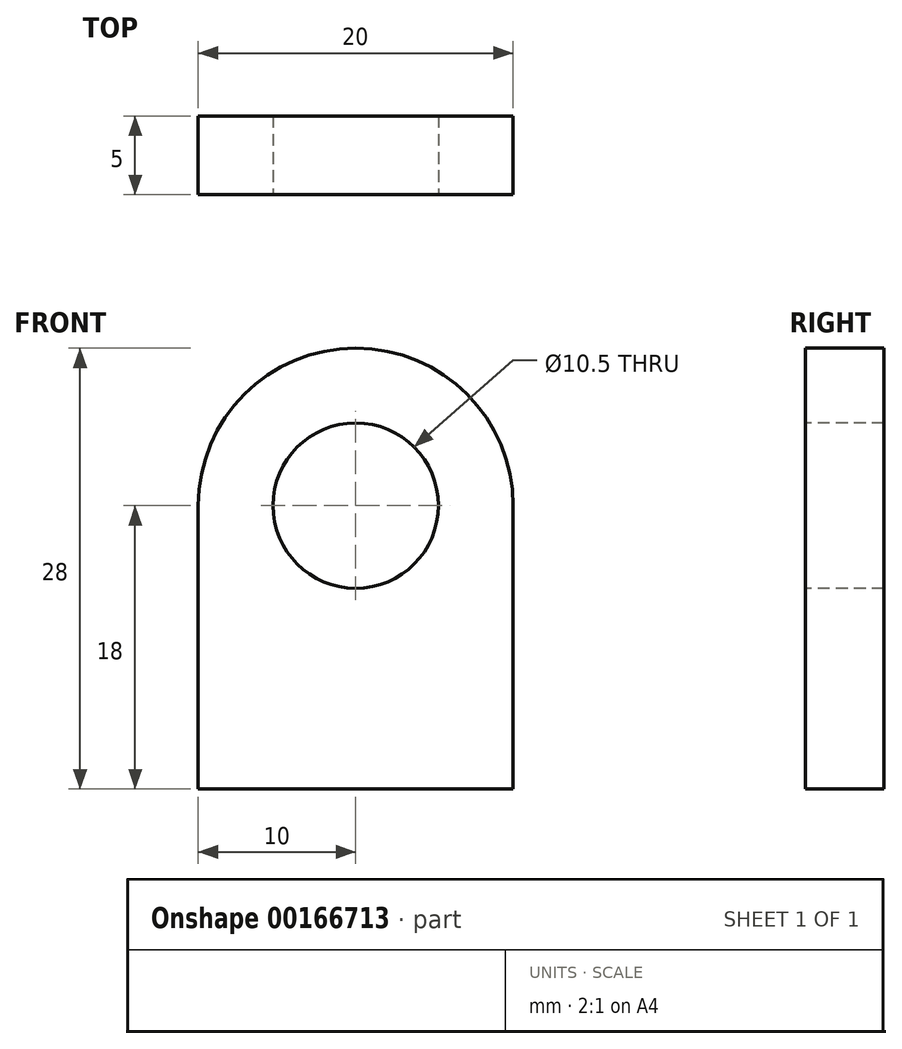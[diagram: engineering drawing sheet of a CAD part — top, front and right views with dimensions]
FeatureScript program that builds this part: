
annotation { "Feature Type Name" : "Feature", "Feature Type Description" : "" }
export const myFeature = defineFeature(function(context is Context, id is Id, definition is map)
    precondition{}
    {
        {
            var Q0;
            Q0=qCreatedBy(makeId("Front.planeOp"),FACE);
            var sketch = newSketch(context, id + "F0", { "sketchPlane" : qUnion([Q0])});
            skCircle(sketch, "E0", {"center": v(0, 0) * mm, "radius": 5.25 * mm});
            skCircle(sketch, "E1", {"center": v(0, 0) * mm, "radius": 10 * mm});
            skLineSegment(sketch, "E2", {"start": v(10, 0) * mm, "end": v(10, -18) * mm});
            skLineSegment(sketch, "E3", {"start": v(10, -18) * mm, "end": v(-10, -18) * mm});
            skLineSegment(sketch, "E4", {"start": v(-10, -18) * mm, "end": v(-10, 0) * mm});
            skSolve(sketch);
        }
        {
            var Q0;
            {var subQ0=sQuery(id+"F0.wireOp",EDGE,"E2");Q0=makeQuery(id+"F0.imprint","IMPRINT",FACE,{"disambiguationData":[TD([[makeQuery(id+"F0.imprint","IMPRINT",EDGE,{"derivedFrom":subQ0}),-1.0]])]});}
            var Q1;
            Q1=makeQuery(id+"F0.imprint","IMPRINT",FACE,{"disambiguationData":[TD([[makeQuery(id+"F0.imprint","IMPRINT",EDGE,{"derivedFrom":sQuery(id+"F0.wireOp",EDGE,"E0")}),-1.0]])]});
            extrude(context, id + "F1", {"entities" : qUnion([Q0, Q1]), "oppositeDirection" : true, "depth" : 5 * mm});
        }
    });
